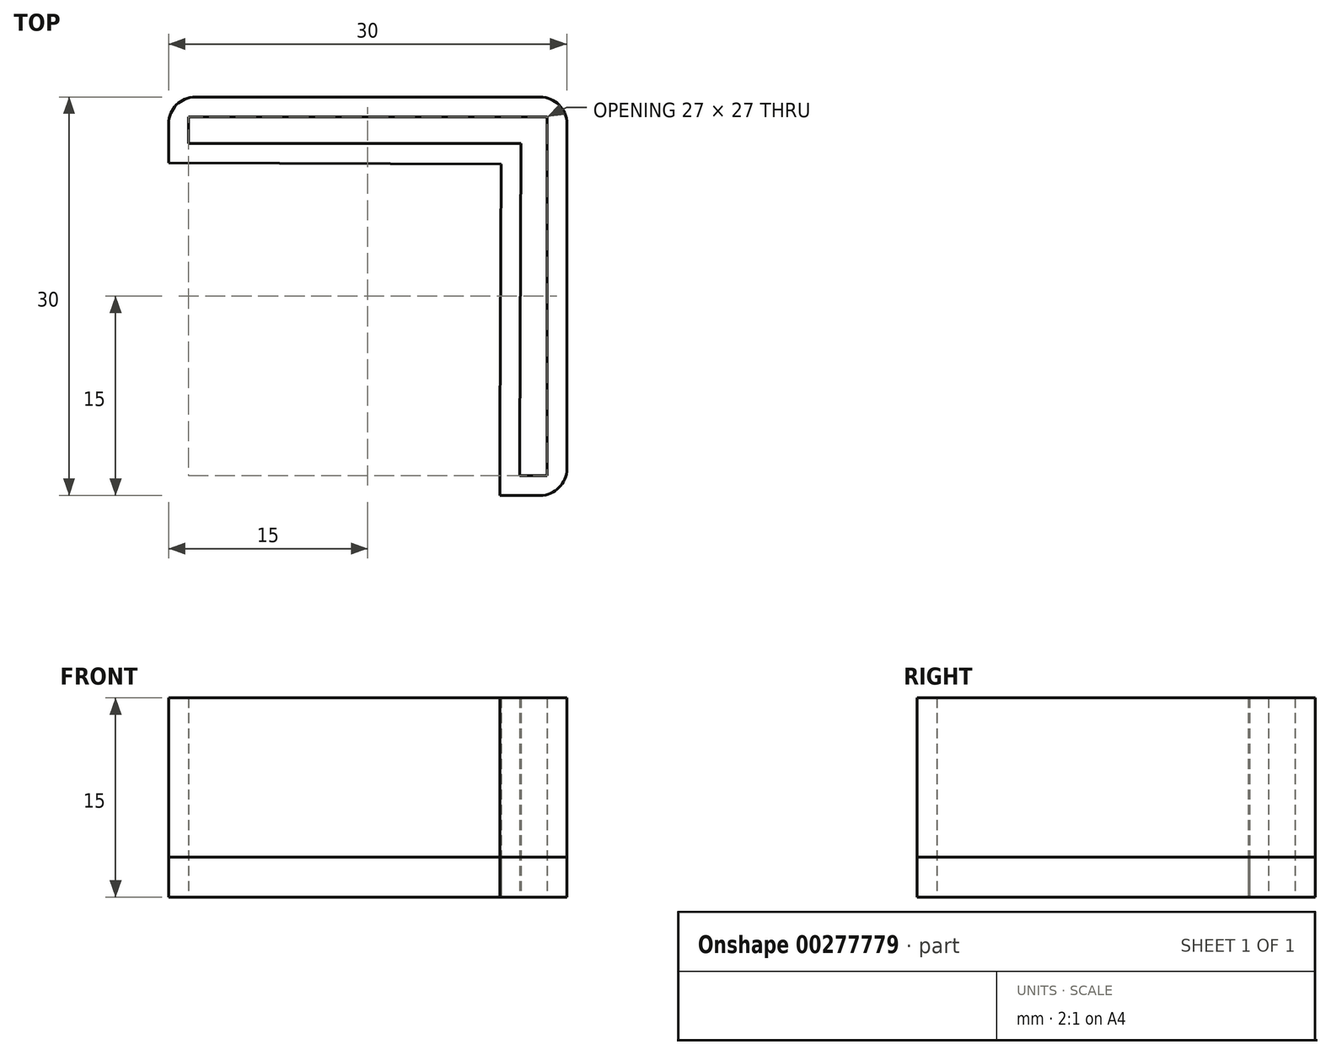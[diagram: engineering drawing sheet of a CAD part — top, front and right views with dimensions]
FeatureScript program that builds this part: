
annotation { "Feature Type Name" : "Feature", "Feature Type Description" : "" }
export const myFeature = defineFeature(function(context is Context, id is Id, definition is map)
    precondition{}
    {
        {
            var Q0;
            Q0=qCreatedBy(makeId("Top.planeOp"),FACE);
            var sketch = newSketch(context, id + "F0", { "sketchPlane" : qUnion([Q0])});
            skLineSegment(sketch, "E0.bottom", {"start": v(-13.5, 13.5) * mm, "end": v(13.5, 13.5) * mm});
            skLineSegment(sketch, "E0.top", {"start": v(11.46, -13.5) * mm, "end": v(13.5, -13.5) * mm});
            skLineSegment(sketch, "E0.left", {"start": v(-13.5, 13.5) * mm, "end": v(-13.5, 11.5) * mm});
            skLineSegment(sketch, "E0.right", {"start": v(13.5, 13.5) * mm, "end": v(13.5, -13.5) * mm});
            skPoint(sketch, "E0.middle", {"position": v(0, 0) * mm});
            skLineSegment(sketch, "E1.bottom", {"start": v(-11.46, 11.5) * mm, "end": v(11.54, 11.5) * mm});
            skLineSegment(sketch, "E1.right", {"start": v(11.54, 11.5) * mm, "end": v(11.46, -11.5) * mm});
            skLineSegment(sketch, "E2", {"start": v(-11.46, 11.5) * mm, "end": v(-13.5, 11.5) * mm});
            skLineSegment(sketch, "E3", {"start": v(11.46, -11.5) * mm, "end": v(11.46, -13.5) * mm});
            skPoint(sketch, "E1.left.end.orphan", {"position": v(-11.54, -11.5) * mm});
            skPoint(sketch, "E4.orphan", {"position": v(-13.5, -13.5) * mm});
            skLineSegment(sketch, "E5.bottom", {"start": v(15, 15) * mm, "end": v(-15, 15) * mm});
            skLineSegment(sketch, "E5.top", {"start": v(15, -15) * mm, "end": v(9.96, -15) * mm});
            skLineSegment(sketch, "E5.left", {"start": v(15, 15) * mm, "end": v(15, -15) * mm});
            skLineSegment(sketch, "E5.right", {"start": v(-15, 15) * mm, "end": v(-15, 10.06) * mm});
            skLineSegment(sketch, "E6.bottom", {"start": v(10.04, 9.96) * mm, "end": v(-9.96, 10.04) * mm});
            skLineSegment(sketch, "E6.left", {"start": v(10.04, 9.96) * mm, "end": v(9.96, -10.04) * mm});
            skLineSegment(sketch, "E7", {"start": v(-9.96, 10.04) * mm, "end": v(-15, 10.06) * mm});
            skLineSegment(sketch, "E8", {"start": v(9.96, -10.04) * mm, "end": v(9.96, -15) * mm});
            skPoint(sketch, "E6.top.end.orphan", {"position": v(-10.04, -9.96) * mm});
            skPoint(sketch, "E9.orphan", {"position": v(-15, -15) * mm});
            skPoint(sketch, "E10", {"position": v(6.75, 6.75) * mm});
            skPoint(sketch, "E11", {"position": v(3.37, 3.37) * mm});
            skCircle(sketch, "E12", {"center": v(3.37, 3.37) * mm, "radius": 21.74 * mm, "construction": true});
            skLineSegment(sketch, "E13.trimOffspring", {"start": v(10.04, 9.96) * mm, "end": v(11.54, 11.5) * mm, "construction": true});
            skCircle(sketch, "E14", {"center": v(3.37, 3.37) * mm, "radius": 23.74 * mm});
            skSolve(sketch);
        }
        {
            var Q0;
            Q0=makeQuery(id+"F0.imprint","IMPRINT",FACE,{"disambiguationData":[TD([[makeQuery(id+"F0.imprint","IMPRINT",EDGE,{"derivedFrom":sQuery(id+"F0.wireOp",EDGE,"E0.bottom")}),1.0]])]});
            var Q1;
            Q1=makeQuery(id+"F0.imprint","IMPRINT",FACE,{"disambiguationData":[TD([[makeQuery(id+"F0.imprint","IMPRINT",EDGE,{"derivedFrom":sQuery(id+"F0.wireOp",EDGE,"E0.bottom")}),-1.0]])]});
            extrude(context, id + "F1", {"entities" : qUnion([Q0, Q1]), "depth" : 3 * mm});
        }
        {
            var Q0;
            Q0=makeQuery(id+"F0.imprint","IMPRINT",FACE,{"disambiguationData":[TD([[makeQuery(id+"F0.imprint","IMPRINT",EDGE,{"derivedFrom":sQuery(id+"F0.wireOp",EDGE,"E0.bottom")}),1.0]])]});
            extrude(context, id + "F2", {"entities" : qUnion([Q0]), "depth" : 15 * mm});
        }
        {
            var Q0;
            Q0=makeQuery(id+"F2.opExtrude","SWEPT_EDGE",EDGE,{"disambiguationData":[OSD([sQuery(id+"F0.wireOp",EDGE,"E5.top"),sQuery(id+"F0.wireOp",EDGE,"E5.left")])]});
            var Q1;
            Q1=makeQuery(id+"F2.opExtrude","SWEPT_EDGE",EDGE,{"disambiguationData":[OSD([sQuery(id+"F0.wireOp",EDGE,"E5.bottom"),sQuery(id+"F0.wireOp",EDGE,"E5.right")])]});
            var Q2;
            Q2=makeQuery(id+"F2.opExtrude","SWEPT_EDGE",EDGE,{"disambiguationData":[OSD([sQuery(id+"F0.wireOp",EDGE,"E5.bottom"),sQuery(id+"F0.wireOp",EDGE,"E5.left")])]});
            fillet(context, id + "F3", {"entities" : qUnion([Q0, Q1, Q2]), "radius" : 2 * mm, "tangentPropagation" : true, "allowEdgeOverflow" : false});
        }
        {
            var Q0;
            Q0=makeQuery(id+"F1.opExtrude","SWEPT_EDGE",EDGE,{"disambiguationData":[OSD([sQuery(id+"F0.wireOp",EDGE,"E5.bottom"),sQuery(id+"F0.wireOp",EDGE,"E5.left")])]});
            var Q1;
            Q1=makeQuery(id+"F1.opExtrude","SWEPT_EDGE",EDGE,{"disambiguationData":[OSD([sQuery(id+"F0.wireOp",EDGE,"E5.top"),sQuery(id+"F0.wireOp",EDGE,"E5.left")])]});
            var Q2;
            Q2=makeQuery(id+"F1.opExtrude","SWEPT_EDGE",EDGE,{"disambiguationData":[OSD([sQuery(id+"F0.wireOp",EDGE,"E5.bottom"),sQuery(id+"F0.wireOp",EDGE,"E5.right")])]});
            fillet(context, id + "F4", {"entities" : qUnion([Q0, Q1, Q2]), "radius" : 2 * mm, "tangentPropagation" : true, "allowEdgeOverflow" : false});
        }
    });
